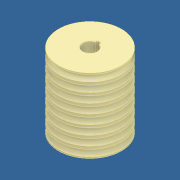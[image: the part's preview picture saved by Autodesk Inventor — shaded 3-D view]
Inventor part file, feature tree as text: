
AUTODESK INVENTOR PART (.ipt)
format: ipt  version: 2018 (Build 220112000, 112)  size: 292,864 bytes
history: native  units: mm
features: sketch x4, extrude x3, revolve x1
ambient origin geometry x8: Origin, YZ Plane, XZ Plane, XY Plane, X Axis, Y Axis, Z Axis, Center Point
bodies: Solid1 (feature_tree)
feature tree (8):
  extrude  "Extrusion1"  Depth=34.0mm
  extrude  "Extrusion2"  Depth=10.0mm TaperAngle=0.0deg
  extrude  "Extrusion3"  Depth=8.0mm
  revolve  "Revolution1"  Angle=360.0deg
  sketch  "Sketch1"  dims[d0=8.0mm d1=34.0mm]
  sketch  "Sketch2"  dims[d2=40.0mm d3=0.0mm d7=10.0mm d8=0.0mm]
  sketch  "Sketch3"  dims[d9=7.0mm d10=8.0mm]
  sketch  "Sketch4"  dims[d11=3.5mm d12=120.0mm d14=360.0deg d16=10.0mm d17=0.0mm d18=2.5mm d19=3.5mm d20=80.0mm d22=5.0mm d23=10.0mm d25=10.0mm d27=34.0mm d28=90.0deg d31=2.0mm d32=1.0mm d33=4.0mm d34=1.0mm]
